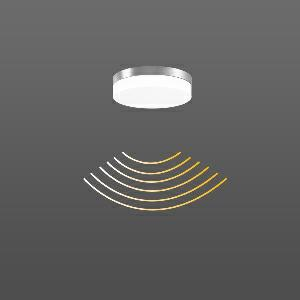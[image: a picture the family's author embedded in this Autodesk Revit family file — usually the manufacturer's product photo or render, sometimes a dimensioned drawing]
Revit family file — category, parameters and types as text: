
# Revit family: flat_slim_round_312135_004_3_19_4290
name_source: partatom
category: Lighting Fixtures
units: mm (PartAtom-declared; Revit-internal decimal feet)

## family parameters
Cut with Voids When Loaded = No
Host = Face
Light Source = No
Part Type = Normal
Room Calculation Point = No
Round Connector Dimension = Use Diameter
Shared = No

## types (1)
- FLAT SLIM round (1 x LED Modul 840, 1300 lm, 4000)
    Apparent Load = 12 VA
    CIE Flux Codes = 43 74 92 91 100
    Color Rendering = 80
    Color Temperature = 4000
    Default Elevation = 1800 mm
    Height = 63 mm
    Lamp = 1 x LED Modul 840
    Lamp Light Flux = 1300 lm
    Lamp count = 1
    Length = 230 mm
    Lifetime = 50000 h
    Luminous efficacy = 108 lm/W
    Manufacturer = RZB
    ModVariant = No
    Model = 312135.004.3.19
    Mounting Place = Ceiling, Wall
    Mounting Type = Surface mounted
    Number of Poles = 1
    OnlyDefault = Yes
    Power Factor = 1
    Product Name = FLAT SLIM round
    Product group = Surface mounted ceiling and wall luminaires
    ProductGroupID = 305
    Protection Class = Protection class I
    Protection Degree = IP 65
    RLX_Detail_Level = 1
    RLX_Emergency_Light_Flux = 0 lm
    RLX_Emergency_Type = 0
    RLX_Emergency_Type_DB = No
    RlxData = <blob elided: 32161 chars, md5=f8ebe6a9>
    Socket = socket
    Standby Power = 0 W
    System Light Flux = 1300 lm
    System Power = 12 W
    Type Comments = Product without accessories
    Type Image = 312132.004.19.jpg
    URL = http://relux.com
    VarID = ---
    Voltage = 230 V
    Voltage Range = 220-240 V
    Weight = 0.00 kg
    Width = 0 mm  [stored 0 ft]

note: [stored X ft] marks values corroborated as IEEE doubles in the binary element streams (Revit-internal decimal feet)

## geometry (parser evidence)
native form markers: Blend x4, Sweep x11
no freeform markers — native parametric forms only
